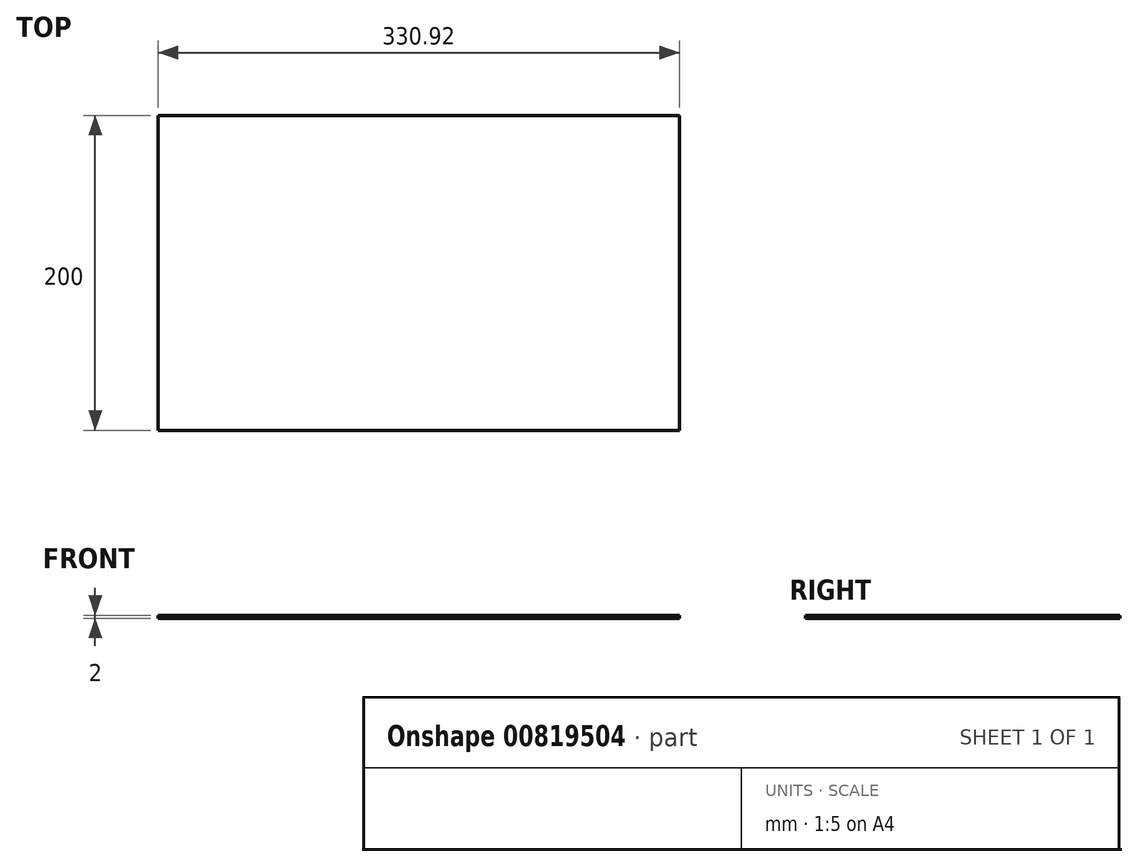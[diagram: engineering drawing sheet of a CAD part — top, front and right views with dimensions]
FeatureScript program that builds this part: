
annotation { "Feature Type Name" : "Feature", "Feature Type Description" : "" }
export const myFeature = defineFeature(function(context is Context, id is Id, definition is map)
    precondition{}
    {
        {
            var Q0;
            Q0=qCreatedBy(makeId("Top.planeOp"),FACE);
            var sketch = newSketch(context, id + "F0", { "sketchPlane" : qUnion([Q0])});
            skLineSegment(sketch, "E0.bottom", {"start": v(173.1, -100) * mm, "end": v(-157.83, -100) * mm});
            skLineSegment(sketch, "E0.top", {"start": v(173.1, 100) * mm, "end": v(-157.83, 100) * mm});
            skLineSegment(sketch, "E0.left", {"start": v(173.1, -100) * mm, "end": v(173.1, 100) * mm});
            skLineSegment(sketch, "E0.right", {"start": v(-157.83, -100) * mm, "end": v(-157.83, 100) * mm});
            skPoint(sketch, "E0.middle", {"position": v(7.63, 0) * mm});
            skSolve(sketch);
        }
        {
            var Q0;
            Q0=makeQuery(id+"F0.imprint","IMPRINT",FACE,{"disambiguationData":[TD([[makeQuery(id+"F0.imprint","IMPRINT",EDGE,{"derivedFrom":sQuery(id+"F0.wireOp",EDGE,"E0.bottom")}),-1.0]])]});
            var sketch = newSketch(context, id + "F1", { "sketchPlane" : qUnion([Q0])});
            skSolve(sketch);
        }
        {
            var Q0;
            Q0=makeQuery(id+"F0.imprint","IMPRINT",FACE,{"disambiguationData":[TD([[makeQuery(id+"F0.imprint","IMPRINT",EDGE,{"derivedFrom":sQuery(id+"F0.wireOp",EDGE,"E0.bottom")}),-1.0]])]});
            extrude(context, id + "F2", {"entities" : qUnion([Q0]), "depth" : 2 * mm, "offsetDistance" : 25 * mm});
        }
    });
